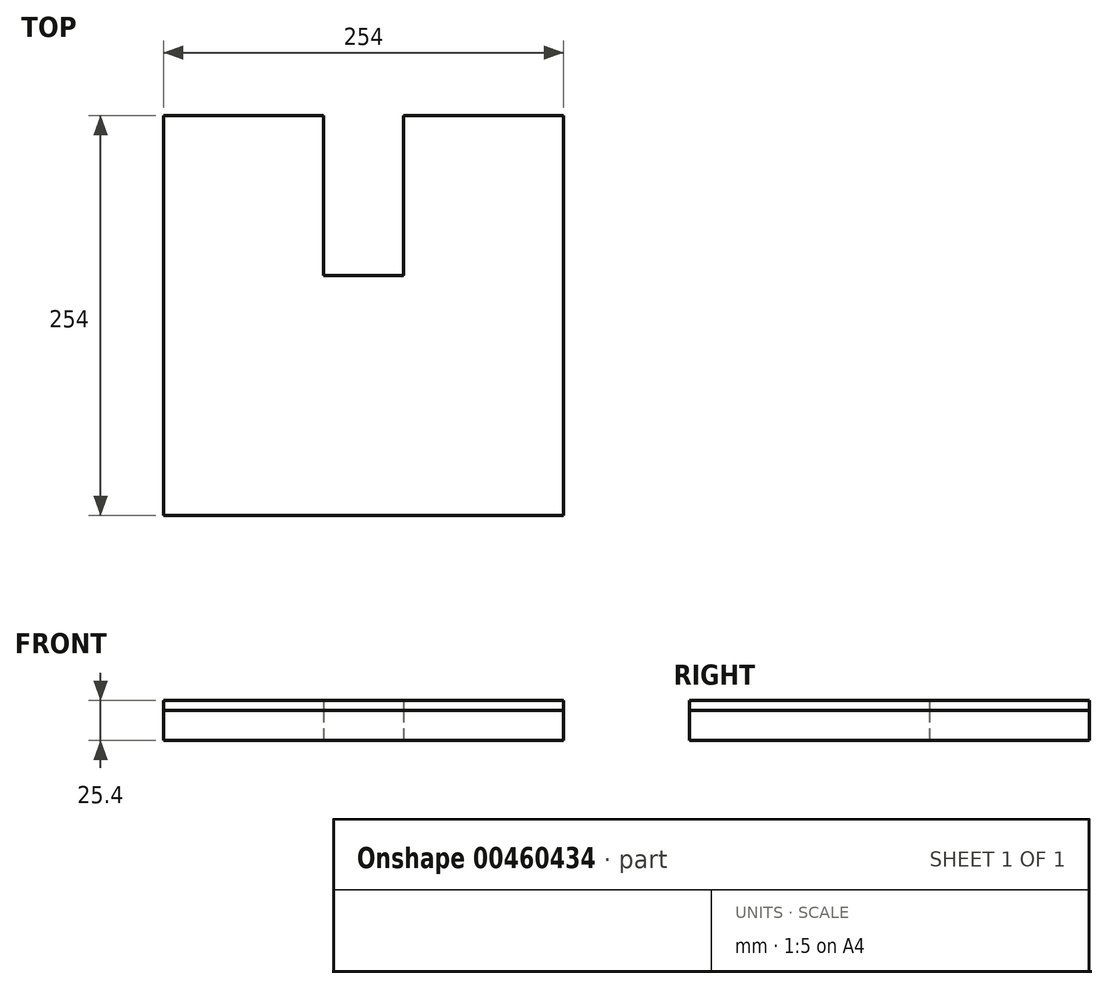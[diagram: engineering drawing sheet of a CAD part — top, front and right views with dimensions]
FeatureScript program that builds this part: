
annotation { "Feature Type Name" : "Feature", "Feature Type Description" : "" }
export const myFeature = defineFeature(function(context is Context, id is Id, definition is map)
    precondition{}
    {
        {
            var Q0;
            Q0=qCreatedBy(makeId("Top.planeOp"),FACE);
            var sketch = newSketch(context, id + "F0", { "sketchPlane" : qUnion([Q0])});
            skLineSegment(sketch, "E0.bottom", {"start": v(0, 0) * mm, "end": v(254, 0) * mm});
            skLineSegment(sketch, "E0.top", {"start": v(0, 254) * mm, "end": v(254, 254) * mm});
            skLineSegment(sketch, "E0.left", {"start": v(0, 0) * mm, "end": v(0, 254) * mm});
            skLineSegment(sketch, "E0.right", {"start": v(254, 0) * mm, "end": v(254, 254) * mm});
            skLineSegment(sketch, "E1", {"start": v(101.6, 254) * mm, "end": v(101.6, 152.4) * mm});
            skLineSegment(sketch, "E2", {"start": v(101.6, 152.4) * mm, "end": v(152.4, 152.4) * mm});
            skLineSegment(sketch, "E3", {"start": v(152.4, 152.4) * mm, "end": v(152.4, 254) * mm});
            skLineSegment(sketch, "E4", {"start": v(127, 254) * mm, "end": v(127, 224.78) * mm, "construction": true});
            skSolve(sketch);
        }
        {
            var Q0;
            Q0=makeQuery(id+"F0.imprint","IMPRINT",FACE,{"disambiguationData":[TD([[makeQuery(id+"F0.imprint","IMPRINT",EDGE,{"derivedFrom":sQuery(id+"F0.wireOp",EDGE,"E0.bottom")}),1.0]])]});
            extrude(context, id + "F1", {"entities" : qUnion([Q0]), "depth" : 19.05 * mm});
        }
        {
            var Q0;
            Q0=makeQuery(id+"F1.opExtrude","CAP_FACE",FACE,{"disambiguationData":[OSD([sQuery(id+"F0.wireOp",EDGE,"E0.bottom"),sQuery(id+"F0.wireOp",EDGE,"E0.top"),sQuery(id+"F0.wireOp",EDGE,"E0.left"),sQuery(id+"F0.wireOp",EDGE,"E0.right"),sQuery(id+"F0.wireOp",EDGE,"E1"),sQuery(id+"F0.wireOp",EDGE,"E2"),sQuery(id+"F0.wireOp",EDGE,"E3")])],"isStart":false});
            extrude(context, id + "F2", {"entities" : qUnion([Q0]), "depth" : 6.35 * mm});
        }
    });
